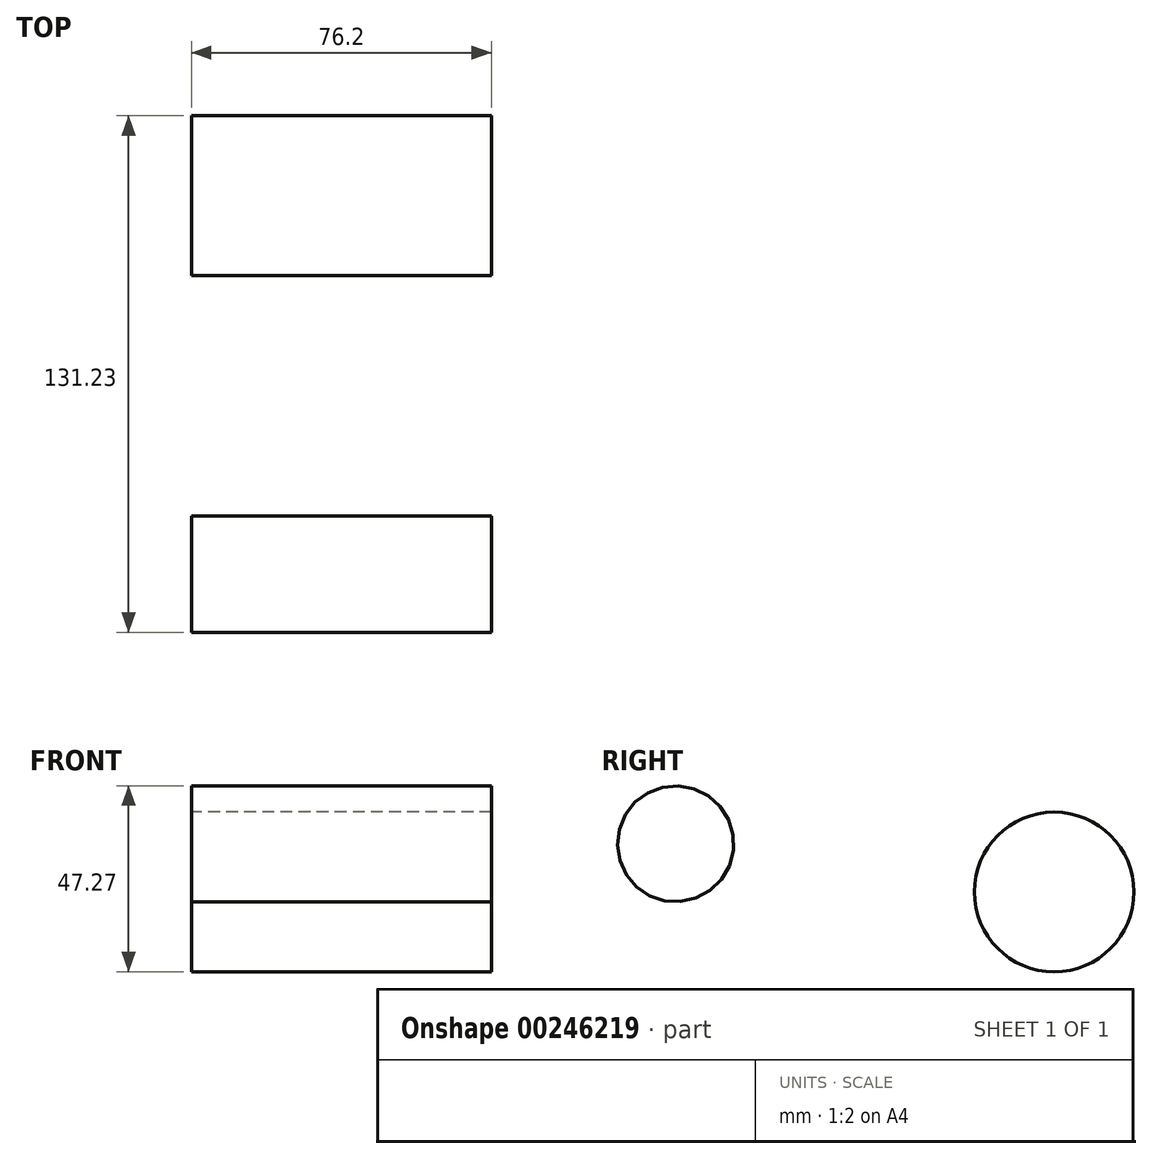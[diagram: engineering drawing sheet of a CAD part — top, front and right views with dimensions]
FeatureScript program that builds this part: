
annotation { "Feature Type Name" : "Feature", "Feature Type Description" : "" }
export const myFeature = defineFeature(function(context is Context, id is Id, definition is map)
    precondition{}
    {
        {
            var Q0;
            Q0=qCreatedBy(makeId("Right.planeOp"),FACE);
            var sketch = newSketch(context, id + "F0", { "sketchPlane" : qUnion([Q0])});
            skCircle(sketch, "E0", {"center": v(40.8, 28.42) * mm, "radius": 20.28 * mm});
            skSolve(sketch);
        }
        {
            var Q0;
            Q0=makeQuery(id+"F0.imprint","IMPRINT",FACE,{"disambiguationData":[TD([[makeQuery(id+"F0.imprint","IMPRINT",EDGE,{"derivedFrom":sQuery(id+"F0.wireOp",EDGE,"E0")}),1.0]])]});
            extrude(context, id + "F1", {"entities" : qUnion([Q0]), "depth" : 76.2 * mm});
        }
        {
            var Q0;
            Q0=qCreatedBy(makeId("Right.planeOp"),FACE);
            var sketch = newSketch(context, id + "F2", { "sketchPlane" : qUnion([Q0])});
            skEllipse(sketch, "E1", {"center": v(-55.38, 40.66) * mm, "majorRadius": 14.74 * mm, "minorRadius": 14.78 * mm, "majorAxis": v(0.42, -0.9)});
            skSolve(sketch);
        }
        {
            var Q0;
            Q0 = qSketchRegion(id + "F2", true);
            extrude(context, id + "F3", {"entities" : qUnion([Q0]), "depth" : 76.2 * mm});
        }
    });
